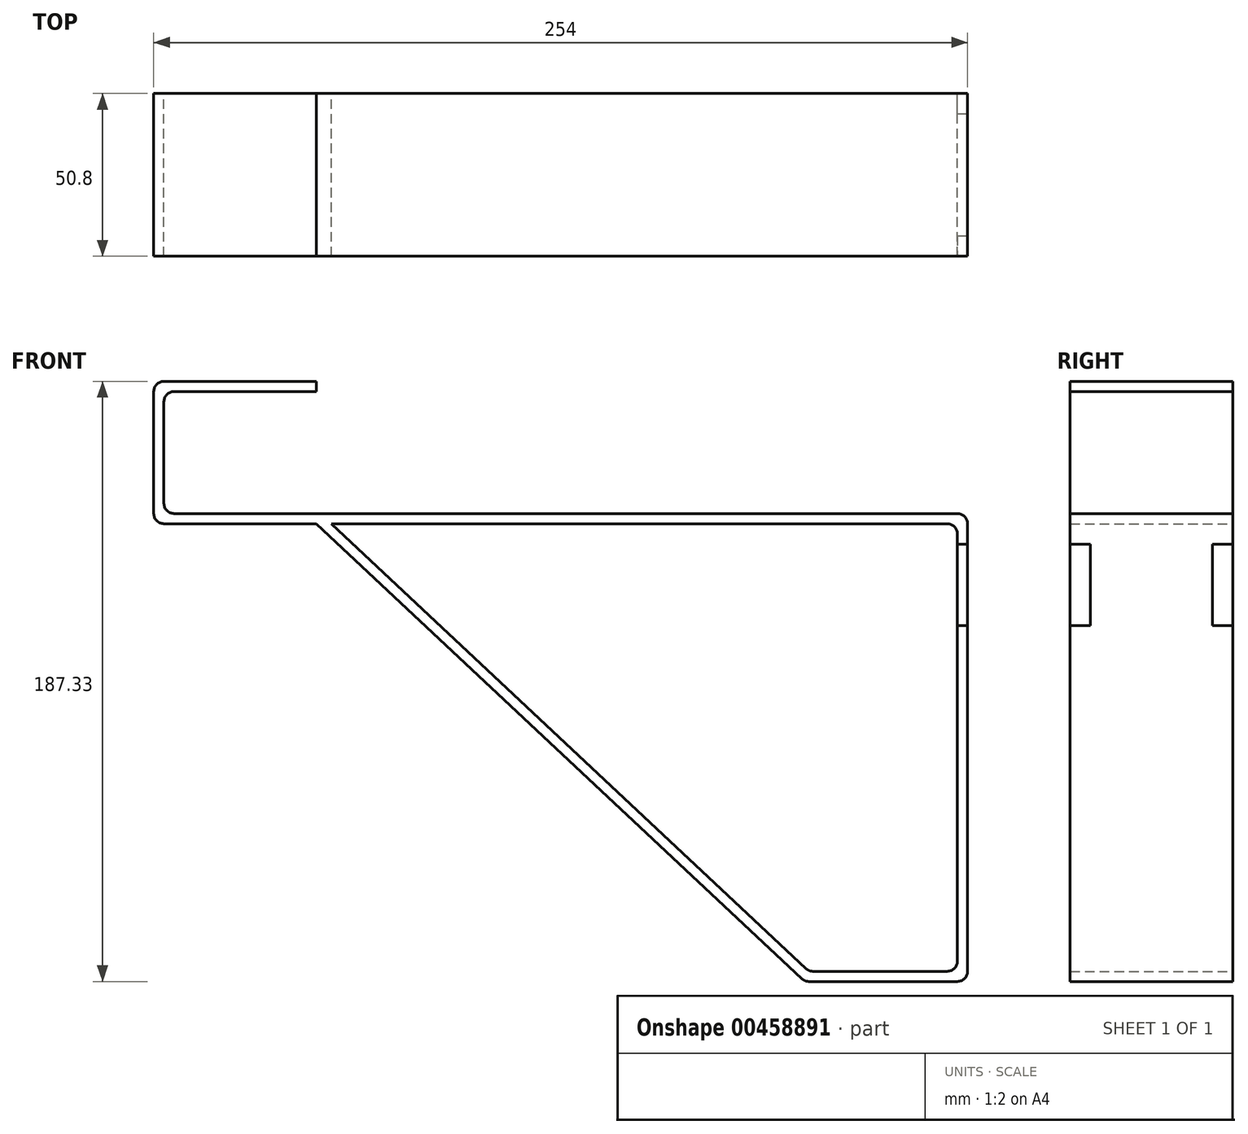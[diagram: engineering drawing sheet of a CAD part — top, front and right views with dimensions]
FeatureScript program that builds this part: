
annotation { "Feature Type Name" : "Feature", "Feature Type Description" : "" }
export const myFeature = defineFeature(function(context is Context, id is Id, definition is map)
    precondition{}
    {
        {
            var Q0;
            Q0=qCreatedBy(makeId("Front.planeOp"),FACE);
            var sketch = newSketch(context, id + "F0", { "sketchPlane" : qUnion([Q0])});
            skLineSegment(sketch, "E0", {"start": v(86.77, 40.18) * mm, "end": v(86.77, -99.52) * mm});
            skLineSegment(sketch, "E1", {"start": v(-160.88, 43.35) * mm, "end": v(-160.88, 81.45) * mm});
            skLineSegment(sketch, "E2", {"start": v(-160.88, 81.45) * mm, "end": v(-113.25, 81.45) * mm});
            skLineSegment(sketch, "E3", {"start": v(-113.25, 81.45) * mm, "end": v(-113.25, 84.63) * mm});
            skLineSegment(sketch, "E4", {"start": v(-113.25, 84.63) * mm, "end": v(-164.05, 84.63) * mm});
            skLineSegment(sketch, "E5", {"start": v(-164.05, 84.63) * mm, "end": v(-164.05, 40.18) * mm});
            skLineSegment(sketch, "E6", {"start": v(-164.05, 40.18) * mm, "end": v(-113.25, 40.18) * mm});
            skLineSegment(sketch, "E7", {"start": v(39.15, -102.7) * mm, "end": v(89.95, -102.7) * mm});
            skLineSegment(sketch, "E8", {"start": v(89.95, 43.35) * mm, "end": v(89.95, -102.7) * mm});
            skLineSegment(sketch, "E9", {"start": v(-160.88, 43.35) * mm, "end": v(89.95, 43.35) * mm});
            skLineSegment(sketch, "E10", {"start": v(-113.25, 40.18) * mm, "end": v(39.15, -102.7) * mm});
            skLineSegment(sketch, "E11", {"start": v(86.77, -99.52) * mm, "end": v(40.4, -99.52) * mm});
            skLineSegment(sketch, "E12", {"start": v(-108.6, 40.18) * mm, "end": v(40.4, -99.52) * mm});
            skLineSegment(sketch, "E13", {"start": v(86.77, 40.18) * mm, "end": v(-108.6, 40.18) * mm});
            skSolve(sketch);
        }
        {
            var Q0;
            Q0=makeQuery(id+"F0.imprint","IMPRINT",FACE,{"disambiguationData":[TD([[makeQuery(id+"F0.imprint","IMPRINT",EDGE,{"derivedFrom":sQuery(id+"F0.wireOp",EDGE,"E0")}),1.0]])]});
            extrude(context, id + "F1", {"entities" : qUnion([Q0]), "depth" : 50.8 * mm});
        }
        {
            var Q0;
            Q0=makeQuery(id+"F1.opExtrude","SWEPT_EDGE",EDGE,{"disambiguationData":[OSD([sQuery(id+"F0.wireOp",EDGE,"E4"),sQuery(id+"F0.wireOp",EDGE,"E5")])]});
            var Q1;
            Q1=makeQuery(id+"F1.opExtrude","SWEPT_EDGE",EDGE,{"disambiguationData":[OSD([sQuery(id+"F0.wireOp",EDGE,"E1"),sQuery(id+"F0.wireOp",EDGE,"E9")])]});
            var Q2;
            Q2=makeQuery(id+"F1.opExtrude","SWEPT_EDGE",EDGE,{"disambiguationData":[OSD([sQuery(id+"F0.wireOp",EDGE,"E8"),sQuery(id+"F0.wireOp",EDGE,"E9")])]});
            var Q3;
            Q3=makeQuery(id+"F1.opExtrude","SWEPT_EDGE",EDGE,{"disambiguationData":[OSD([sQuery(id+"F0.wireOp",EDGE,"E7"),sQuery(id+"F0.wireOp",EDGE,"E8")])]});
            var Q4;
            Q4=makeQuery(id+"F1.opExtrude","SWEPT_EDGE",EDGE,{"disambiguationData":[OSD([sQuery(id+"F0.wireOp",EDGE,"E5"),sQuery(id+"F0.wireOp",EDGE,"E6")])]});
            var Q5;
            Q5=makeQuery(id+"F1.opExtrude","SWEPT_EDGE",EDGE,{"disambiguationData":[OSD([sQuery(id+"F0.wireOp",EDGE,"E0"),sQuery(id+"F0.wireOp",EDGE,"tUMfCN4a-LukW-TJge-6rHA-w5qocvdWwtkP")])]});
            var Q6;
            Q6=makeQuery(id+"F1.opExtrude","SWEPT_EDGE",EDGE,{"disambiguationData":[OSD([sQuery(id+"F0.wireOp",EDGE,"E1"),sQuery(id+"F0.wireOp",EDGE,"E2")])]});
            var Q7;
            Q7=makeQuery(id+"F1.opExtrude","SWEPT_EDGE",EDGE,{"disambiguationData":[OSD([sQuery(id+"F0.wireOp",EDGE,"E7"),sQuery(id+"F0.wireOp",EDGE,"E10")])]});
            var Q8;
            Q8=makeQuery(id+"F1.opExtrude","SWEPT_EDGE",EDGE,{"disambiguationData":[OSD([sQuery(id+"F0.wireOp",EDGE,"cMELWity-YZMI-lv4l-rxWX-igUgAkN2WnPw"),sQuery(id+"F0.wireOp",EDGE,"tUMfCN4a-LukW-TJge-6rHA-w5qocvdWwtkP")])]});
            var Q9;
            Q9=makeQuery(id+"F1.opExtrude","SWEPT_EDGE",EDGE,{"disambiguationData":[OSD([sQuery(id+"F0.wireOp",EDGE,"E0"),sQuery(id+"F0.wireOp",EDGE,"SNwB0gLn-Ef8P-Q0Ip-ruGg-AWRy9V6pnG0R")])]});
            fillet(context, id + "F2", {"entities" : qUnion([Q0, Q1, Q2, Q3, Q4, Q5, Q6, Q7, Q8, Q9]), "radius" : 3.17 * mm, "tangentPropagation" : true, "allowEdgeOverflow" : false});
        }
        {
            var Q0;
            Q0=makeQuery(id+"F1.opExtrude","SWEPT_EDGE",EDGE,{"disambiguationData":[OSD([sQuery(id+"F0.wireOp",EDGE,"E11"),sQuery(id+"F0.wireOp",EDGE,"E12")])]});
            fillet(context, id + "F3", {"entities" : qUnion([Q0]), "radius" : 3.17 * mm, "tangentPropagation" : true, "allowEdgeOverflow" : false});
        }
        {
            var Q0;
            Q0=makeQuery(id+"F1.opExtrude","SWEPT_FACE",FACE,{"disambiguationData":[OSD([sQuery(id+"F0.wireOp",EDGE,"E8")])]});
            var sketch = newSketch(context, id + "F4", { "sketchPlane" : qUnion([Q0])});
            skLineSegment(sketch, "E14", {"start": v(-63.22, 8.43) * mm, "end": v(-63.22, 33.83) * mm});
            skLineSegment(sketch, "E15", {"start": v(-63.22, 33.83) * mm, "end": v(-44.45, 33.83) * mm});
            skLineSegment(sketch, "E16", {"start": v(-44.45, 33.83) * mm, "end": v(-44.45, 8.43) * mm});
            skLineSegment(sketch, "E17", {"start": v(-44.45, 8.43) * mm, "end": v(-63.22, 8.43) * mm});
            skLineSegment(sketch, "E18", {"start": v(-6.35, 8.43) * mm, "end": v(-6.35, 33.83) * mm});
            skLineSegment(sketch, "E19", {"start": v(-6.35, 33.83) * mm, "end": v(12.42, 33.83) * mm});
            skLineSegment(sketch, "E20", {"start": v(12.42, 33.83) * mm, "end": v(12.42, 8.43) * mm});
            skLineSegment(sketch, "E21", {"start": v(12.42, 8.43) * mm, "end": v(-6.35, 8.43) * mm});
            skSolve(sketch);
        }
        {
            var Q0;
            {var subQ0=sQuery(id+"F4.wireOp",EDGE,"E18");Q0=makeQuery(id+"F4.imprint","IMPRINT",FACE,{"disambiguationData":[TD([[makeQuery(id+"F4.imprint","IMPRINT",EDGE,{"derivedFrom":subQ0}),-1.0]])]});}
            var Q1;
            {var subQ0=sQuery(id+"F4.wireOp",EDGE,"E16");Q1=makeQuery(id+"F4.imprint","IMPRINT",FACE,{"disambiguationData":[TD([[makeQuery(id+"F4.imprint","IMPRINT",EDGE,{"derivedFrom":subQ0}),-1.0]])]});}
            extrude(context, id + "F5", {"entities" : qUnion([Q0, Q1]), "operationType" : NewBodyOperationType.REMOVE, "oppositeDirection" : true, "depth" : 25.4 * mm});
        }
    });
